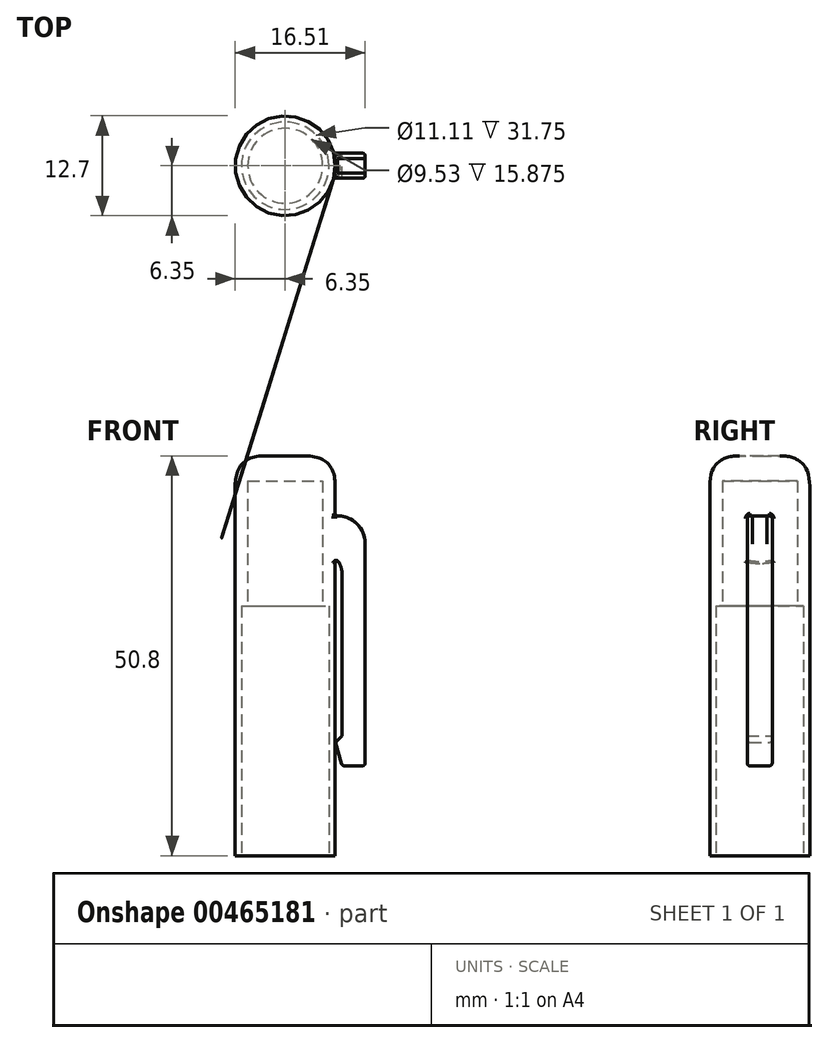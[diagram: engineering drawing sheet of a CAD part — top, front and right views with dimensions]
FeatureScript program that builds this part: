
annotation { "Feature Type Name" : "Feature", "Feature Type Description" : "" }
export const myFeature = defineFeature(function(context is Context, id is Id, definition is map)
    precondition{}
    {
        {
            var Q0;
            Q0=qCreatedBy(makeId("Top.planeOp"),FACE);
            var sketch = newSketch(context, id + "F0", { "sketchPlane" : qUnion([Q0])});
            skCircle(sketch, "E0", {"center": v(0, 0) * mm, "radius": 6.35 * mm});
            skSolve(sketch);
        }
        {
            var Q0;
            Q0=makeQuery(id+"F0.imprint","IMPRINT",FACE,{"disambiguationData":[TD([[makeQuery(id+"F0.imprint","IMPRINT",EDGE,{"derivedFrom":sQuery(id+"F0.wireOp",EDGE,"E0")}),1.0]])]});
            extrude(context, id + "F1", {"entities" : qUnion([Q0]), "endBound" : BoundingType.SYMMETRIC, "depth" : 50.8 * mm});
        }
        {
            var Q0;
            Q0=makeQuery(id+"F1.opExtrude","CAP_EDGE",EDGE,{"disambiguationData":[OSD([sQuery(id+"F0.wireOp",EDGE,"E0")])],"isStart":false});
            fillet(context, id + "F2", {"entities" : qUnion([Q0]), "radius" : 3.8 * mm, "tangentPropagation" : true, "rho" : 0.5, "crossSection" : FilletCrossSection.CONIC, "allowEdgeOverflow" : false});
        }
        {
            var Q0;
            Q0=makeQuery(id+"F1.opExtrude","CAP_FACE",FACE,{"disambiguationData":[OSD([sQuery(id+"F0.wireOp",EDGE,"E0")])],"isStart":true});
            var sketch = newSketch(context, id + "F3", { "sketchPlane" : qUnion([Q0])});
            skCircle(sketch, "E1", {"center": v(0, 0) * mm, "radius": 4.76 * mm});
            skSolve(sketch);
        }
        {
            var Q0;
            Q0=makeQuery(id+"F3.imprint","IMPRINT",FACE,{"disambiguationData":[TD([[makeQuery(id+"F3.imprint","IMPRINT",EDGE,{"derivedFrom":sQuery(id+"F3.wireOp",EDGE,"E1")}),1.0]])]});
            extrude(context, id + "F4", {"entities" : qUnion([Q0]), "operationType" : NewBodyOperationType.REMOVE, "oppositeDirection" : true, "depth" : 47.62 * mm});
        }
        {
            var Q0;
            Q0=makeQuery(id+"F1.opExtrude","CAP_FACE",FACE,{"disambiguationData":[OSD([sQuery(id+"F0.wireOp",EDGE,"E0")])],"isStart":true});
            var sketch = newSketch(context, id + "F5", { "sketchPlane" : qUnion([Q0])});
            skCircle(sketch, "E2", {"center": v(0, 0) * mm, "radius": 5.56 * mm});
            skSolve(sketch);
        }
        {
            var Q0;
            Q0=makeQuery(id+"F5.imprint","IMPRINT",FACE,{"disambiguationData":[TD([[makeQuery(id+"F5.imprint","IMPRINT",EDGE,{"derivedFrom":sQuery(id+"F5.wireOp",EDGE,"E2")}),1.0]])]});
            extrude(context, id + "F6", {"entities" : qUnion([Q0]), "operationType" : NewBodyOperationType.REMOVE, "oppositeDirection" : true, "depth" : 31.75 * mm});
        }
        {
            var Q0;
            Q0=qCreatedBy(makeId("Front.planeOp"),FACE);
            var sketch = newSketch(context, id + "F7", { "sketchPlane" : qUnion([Q0])});
            skLineSegment(sketch, "E3", {"start": v(4.83, 17.78) * mm, "end": v(10.16, 17.78) * mm});
            skLineSegment(sketch, "E4", {"start": v(10.16, 17.78) * mm, "end": v(10.16, -13.97) * mm});
            skLineSegment(sketch, "E5", {"start": v(10.16, -13.97) * mm, "end": v(7.24, -13.97) * mm});
            skLineSegment(sketch, "E6", {"start": v(7.24, 12.7) * mm, "end": v(4.83, 12.7) * mm});
            skLineSegment(sketch, "E7", {"start": v(4.83, 12.7) * mm, "end": v(4.83, 17.78) * mm});
            skLineSegment(sketch, "E8", {"start": v(7.24, -13.97) * mm, "end": v(6.4, -11) * mm});
            skLineSegment(sketch, "E9", {"start": v(6.4, -11) * mm, "end": v(7.24, -10.2) * mm});
            skLineSegment(sketch, "E10", {"start": v(7.24, -10.2) * mm, "end": v(7.24, 12.7) * mm});
            skSolve(sketch);
        }
        {
            var Q0;
            Q0=makeQuery(id+"F7.imprint","IMPRINT",FACE,{"disambiguationData":[TD([[makeQuery(id+"F7.imprint","IMPRINT",EDGE,{"derivedFrom":sQuery(id+"F7.wireOp",EDGE,"E3")}),-1.0]])]});
            extrude(context, id + "F8", {"entities" : qUnion([Q0]), "operationType" : NewBodyOperationType.ADD, "endBound" : BoundingType.SYMMETRIC, "depth" : 3.17 * mm});
        }
        {
            var Q0;
            Q0=makeQuery(id+"F8.opExtrude","SWEPT_EDGE",EDGE,{"disambiguationData":[OSD([sQuery(id+"F7.wireOp",EDGE,"E6"),sQuery(id+"F7.wireOp",EDGE,"E10")])]});
            fillet(context, id + "F9", {"entities" : qUnion([Q0]), "radius" : 3.17 * mm, "tangentPropagation" : true, "allowEdgeOverflow" : false});
        }
        {
            var Q0;
            Q0=makeQuery(id+"F8.opExtrude","CAP_EDGE",EDGE,{"disambiguationData":[OSD([sQuery(id+"F7.wireOp",EDGE,"E8")])],"isStart":false});
            var Q1;
            Q1=makeQuery(id+"F8.opExtrude","CAP_EDGE",EDGE,{"disambiguationData":[OSD([sQuery(id+"F7.wireOp",EDGE,"E5")])],"isStart":false});
            var Q2;
            Q2=makeQuery(id+"F8.opExtrude","SWEPT_EDGE",EDGE,{"disambiguationData":[OSD([sQuery(id+"F7.wireOp",EDGE,"E5"),sQuery(id+"F7.wireOp",EDGE,"E8")])]});
            var Q3;
            Q3=makeQuery(id+"F8.opExtrude","SWEPT_EDGE",EDGE,{"disambiguationData":[OSD([sQuery(id+"F7.wireOp",EDGE,"E4"),sQuery(id+"F7.wireOp",EDGE,"E5")])]});
            var Q4;
            Q4=makeQuery(id+"F8.opExtrude","CAP_EDGE",EDGE,{"disambiguationData":[OSD([sQuery(id+"F7.wireOp",EDGE,"E5")])],"isStart":true});
            var Q5;
            Q5=makeQuery(id+"F8.opExtrude","CAP_EDGE",EDGE,{"disambiguationData":[OSD([sQuery(id+"F7.wireOp",EDGE,"E8")])],"isStart":true});
            var Q6;
            Q6=makeQuery(id+"F8.opExtrude","CAP_EDGE",EDGE,{"disambiguationData":[OSD([sQuery(id+"F7.wireOp",EDGE,"E4")])],"isStart":true});
            var Q7;
            Q7=makeQuery(id+"F8.opExtrude","CAP_EDGE",EDGE,{"disambiguationData":[OSD([sQuery(id+"F7.wireOp",EDGE,"E4")])],"isStart":false});
            var Q8;
            Q8=makeQuery(id+"F8.opExtrude","CAP_EDGE",EDGE,{"disambiguationData":[OSD([sQuery(id+"F7.wireOp",EDGE,"E3")])],"isStart":false});
            var Q9;
            {var subQ0=sQuery(id+"F7.wireOp",EDGE,"E4");var subQ1=sQuery(id+"F7.wireOp",EDGE,"E3");Q9=makeQuery(id+"F9.opFillet","BLEND_EDGE",EDGE,{"blendedFrom":[makeQuery(id+"F8.opExtrude","SWEPT_EDGE",EDGE,{"disambiguationData":[OSD([subQ1,subQ0])]}),makeQuery(id+"F8.opExtrude","CAP_FACE",FACE,{"disambiguationData":[OSD([subQ1,subQ0,sQuery(id+"F7.wireOp",EDGE,"E5"),sQuery(id+"F7.wireOp",EDGE,"E6"),sQuery(id+"F7.wireOp",EDGE,"E7"),sQuery(id+"F7.wireOp",EDGE,"E8"),sQuery(id+"F7.wireOp",EDGE,"E9"),sQuery(id+"F7.wireOp",EDGE,"E10")])],"isStart":false})],"blendedInto":[makeQuery(id+"F8.opExtrude","CAP_FACE",FACE,{"disambiguationData":[OSD([subQ1,subQ0,sQuery(id+"F7.wireOp",EDGE,"E5"),sQuery(id+"F7.wireOp",EDGE,"E6"),sQuery(id+"F7.wireOp",EDGE,"E7"),sQuery(id+"F7.wireOp",EDGE,"E8"),sQuery(id+"F7.wireOp",EDGE,"E9"),sQuery(id+"F7.wireOp",EDGE,"E10")])],"isStart":false})]});}
            var Q10;
            Q10=makeQuery(id+"F8.opExtrude","CAP_EDGE",EDGE,{"disambiguationData":[OSD([sQuery(id+"F7.wireOp",EDGE,"E3")])],"isStart":true});
            var Q11;
            {var subQ0=sQuery(id+"F7.wireOp",EDGE,"E4");var subQ1=sQuery(id+"F7.wireOp",EDGE,"E3");Q11=makeQuery(id+"F9.opFillet","BLEND_EDGE",EDGE,{"blendedFrom":[makeQuery(id+"F8.opExtrude","SWEPT_EDGE",EDGE,{"disambiguationData":[OSD([subQ1,subQ0])]}),makeQuery(id+"F8.opExtrude","CAP_FACE",FACE,{"disambiguationData":[OSD([subQ1,subQ0,sQuery(id+"F7.wireOp",EDGE,"E5"),sQuery(id+"F7.wireOp",EDGE,"E6"),sQuery(id+"F7.wireOp",EDGE,"E7"),sQuery(id+"F7.wireOp",EDGE,"E8"),sQuery(id+"F7.wireOp",EDGE,"E9"),sQuery(id+"F7.wireOp",EDGE,"E10")])],"isStart":true})],"blendedInto":[makeQuery(id+"F8.opExtrude","CAP_FACE",FACE,{"disambiguationData":[OSD([subQ1,subQ0,sQuery(id+"F7.wireOp",EDGE,"E5"),sQuery(id+"F7.wireOp",EDGE,"E6"),sQuery(id+"F7.wireOp",EDGE,"E7"),sQuery(id+"F7.wireOp",EDGE,"E8"),sQuery(id+"F7.wireOp",EDGE,"E9"),sQuery(id+"F7.wireOp",EDGE,"E10")])],"isStart":true})]});}
            var Q12;
            Q12=makeQuery(id+"F8.boolean.opBoolean","INTERSECT",EDGE,{"derivedFrom":[makeQuery(id+"F1.opExtrude","SWEPT_FACE",FACE,{"disambiguationData":[OSD([sQuery(id+"F0.wireOp",EDGE,"E0")])]}),makeQuery(id+"F8.opExtrude","CAP_FACE",FACE,{"disambiguationData":[OSD([sQuery(id+"F7.wireOp",EDGE,"E3"),sQuery(id+"F7.wireOp",EDGE,"E4"),sQuery(id+"F7.wireOp",EDGE,"E5"),sQuery(id+"F7.wireOp",EDGE,"E6"),sQuery(id+"F7.wireOp",EDGE,"E7"),sQuery(id+"F7.wireOp",EDGE,"E8"),sQuery(id+"F7.wireOp",EDGE,"E9"),sQuery(id+"F7.wireOp",EDGE,"E10")])],"isStart":true})]});
            var Q13;
            Q13=makeQuery(id+"F8.boolean.opBoolean","INTERSECT",EDGE,{"derivedFrom":[makeQuery(id+"F1.opExtrude","SWEPT_FACE",FACE,{"disambiguationData":[OSD([sQuery(id+"F0.wireOp",EDGE,"E0")])]}),makeQuery(id+"F8.opExtrude","SWEPT_FACE",FACE,{"disambiguationData":[OSD([sQuery(id+"F7.wireOp",EDGE,"E3")])]})]});
            var Q14;
            Q14=makeQuery(id+"F8.boolean.opBoolean","INTERSECT",EDGE,{"derivedFrom":[makeQuery(id+"F1.opExtrude","SWEPT_FACE",FACE,{"disambiguationData":[OSD([sQuery(id+"F0.wireOp",EDGE,"E0")])]}),makeQuery(id+"F8.opExtrude","CAP_FACE",FACE,{"disambiguationData":[OSD([sQuery(id+"F7.wireOp",EDGE,"E3"),sQuery(id+"F7.wireOp",EDGE,"E4"),sQuery(id+"F7.wireOp",EDGE,"E5"),sQuery(id+"F7.wireOp",EDGE,"E6"),sQuery(id+"F7.wireOp",EDGE,"E7"),sQuery(id+"F7.wireOp",EDGE,"E8"),sQuery(id+"F7.wireOp",EDGE,"E9"),sQuery(id+"F7.wireOp",EDGE,"E10")])],"isStart":false})]});
            var Q15;
            Q15=makeQuery(id+"F9.opFillet","BLEND_EDGE",EDGE,{"blendedFrom":[makeQuery(id+"F8.opExtrude","SWEPT_EDGE",EDGE,{"disambiguationData":[OSD([sQuery(id+"F7.wireOp",EDGE,"E6"),sQuery(id+"F7.wireOp",EDGE,"E10")])]}),makeQuery(id+"F1.opExtrude","SWEPT_FACE",FACE,{"disambiguationData":[OSD([sQuery(id+"F0.wireOp",EDGE,"E0")])]})],"blendedInto":[makeQuery(id+"F1.opExtrude","SWEPT_FACE",FACE,{"disambiguationData":[OSD([sQuery(id+"F0.wireOp",EDGE,"E0")])]})]});
            fillet(context, id + "F10", {"entities" : qUnion([Q0, Q1, Q2, Q3, Q4, Q5, Q6, Q7, Q8, Q9, Q10, Q11, Q12, Q13, Q14, Q15]), "radius" : 0.32 * mm, "allowEdgeOverflow" : false});
        }
        {
            var Q0;
            Q0=makeQuery(id+"F8.opExtrude","SWEPT_EDGE",EDGE,{"disambiguationData":[OSD([sQuery(id+"F7.wireOp",EDGE,"E3"),sQuery(id+"F7.wireOp",EDGE,"E4")])]});
            fillet(context, id + "F11", {"entities" : qUnion([Q0]), "radius" : 3.56 * mm, "tangentPropagation" : true, "allowEdgeOverflow" : false});
        }
    });
